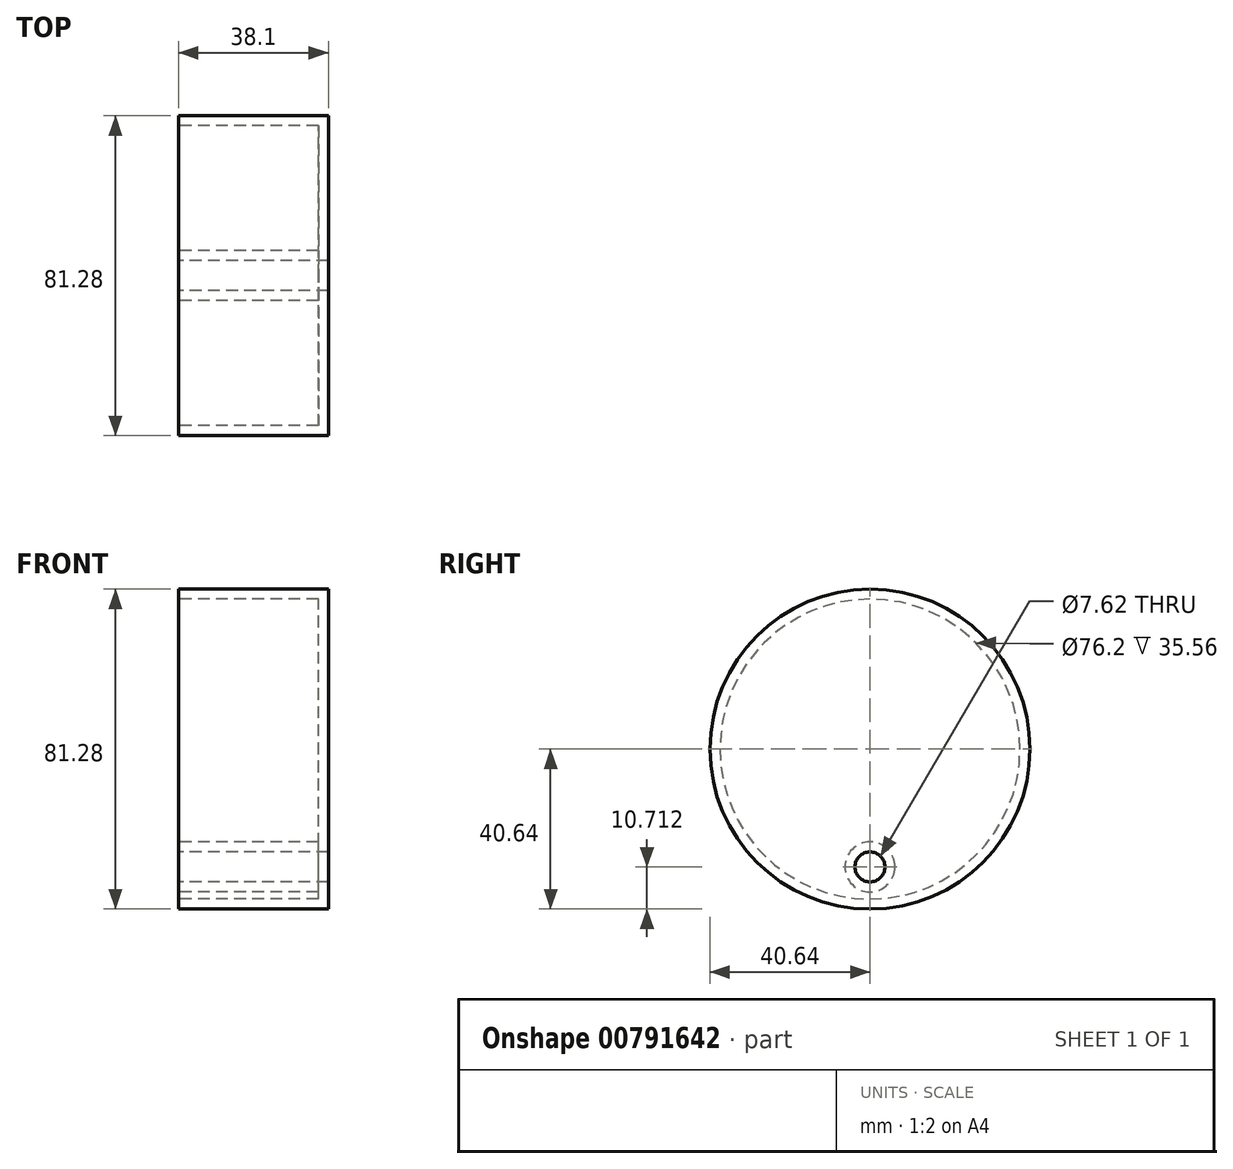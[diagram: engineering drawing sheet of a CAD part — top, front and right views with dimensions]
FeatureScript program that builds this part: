
annotation { "Feature Type Name" : "Feature", "Feature Type Description" : "" }
export const myFeature = defineFeature(function(context is Context, id is Id, definition is map)
    precondition{}
    {
        {
            var Q0;
            Q0=qCreatedBy(makeId("Right.planeOp"),FACE);
            var sketch = newSketch(context, id + "F0", { "sketchPlane" : qUnion([Q0])});
            skCircle(sketch, "E0", {"center": v(0, 0) * mm, "radius": 40.64 * mm});
            skCircle(sketch, "E1", {"center": v(0, -29.93) * mm, "radius": 3.81 * mm});
            skSolve(sketch);
        }
        {
            var Q0;
            Q0 = qSketchRegion(id + "F0", true);
            extrude(context, id + "F1", {"entities" : qUnion([Q0]), "depth" : 38.1 * mm, "offsetDistance" : 25.4 * mm});
        }
        {
            var Q0;
            Q0=makeQuery(id+"F1.opExtrude","CAP_FACE",FACE,{"disambiguationData":[OSD([sQuery(id+"F0.wireOp",EDGE,"E0")])],"isStart":true});
            shell(context, id + "F2", {"entities" : qUnion([Q0]), "thickness" : 2.54 * mm});
        }
    });
